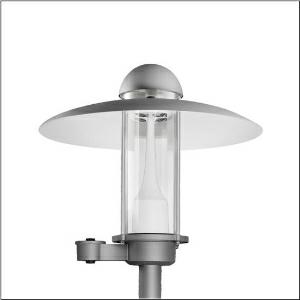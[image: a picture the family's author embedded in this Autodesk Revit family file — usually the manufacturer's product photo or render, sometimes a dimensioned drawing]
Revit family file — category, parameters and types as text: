
# Revit family: city-light_elegance___st1_2a_5xa5263er14h000032_c7d7
name_source: partatom
category: Lighting Fixtures
units: mm (PartAtom-declared; Revit-internal decimal feet)

## family parameters
Cut with Voids When Loaded = No
Host = Face
Light Source = No
Part Type = Normal
Room Calculation Point = No
Round Connector Dimension = Use Diameter
Shared = No

## types (1)
- --- (1 x LED, 1470 lm, 14.2 W, 3000K)
    Apparent Load = 14 VA
    CIE Flux Codes = 22 62 94 98 100
    Color Rendering = 80
    Color Temperature = 3000K
    Default Elevation = 1800 mm
    Description = City-Light Elegance, mast luminaire, Module 540 Plus, primary light control with 3 zone facetted reflector, of plastic, silver coated, highly specular, structured, primary optical cover: cover, of PMMA, transparent, light distribution: ST1.2a, light emission: direct distribution, primary light characteristic: asymmetric, installation type: post-top, LED, High Power LED, rated luminous flux: 1.470lm, luminous efficacy: 104lm/W, light colour: 730, colour temperature: 3000K, control gear: ECG Smart Interface, control: overheat protection, digital communication interface, time-dependent luminous flux control, flexible luminous flux parameterisation, presetting dimming logarithmic, with terminal, 6-pole, max. 2.5mm², mains connection: 220..240V, AC, 50/60Hz, start of lifetime: 14W, end of lifetime: 15W, reduction: 8W, luminaire housing, upper part, of aluminium, coated, Siteco® metallic grey (DB 702S), diameter: 750mm, height: 675mm, spigot size: d x l = 76 x 70mm (post-top) | with reducer (optional accessory) 60 x 70mm, post-top mast mounting element, of diecast aluminium, coated, Siteco® metallic grey (DB 702S), Module 540 Plus, traffic white (RAL 9016), protection rating (complete): IP65, insulation class (complete): insulation class II (safety insulation), certification: CE, ENEC, VDE, packaging unit: 1 piece

Light Distribution: ST1.2a
    Height = 675 mm
    Lamp = 1 x LED
    Lamp Light Flux = 1470 lm
    Lamp Power = 14.2 W
    Lamp count = 1
    Length = 750 mm
    Luminous efficacy = 104 lm/W
    Manufacturer = Siteco
    ModVariant = No
    Model = 5XA5263ER14H000032
    Number of Poles = 1
    OnlyDefault = Yes
    Power Factor = 1
    Product Name = City-Light Elegance | ST1.2a
    Product group = mast luminaire | pylon top
    ProductGroupID = 6100
    Protection Class = Protection class II
    Protection Degree = IP 65
    RLX_Detail_Level = 1
    RlxData = <blob elided: 72309 chars, md5=f19250c3>
    Socket = socket
    Standby Power = 0 W
    System Light Flux = 1470 lm
    System Power = 14 W
    Type Comments = factory setting: luminous flux: 100 % | dim-lin: 254 | 516 mA
    Type Image = l_1005991.jpg
    URL = http://relux.com
    VarID = @adj_121759
    Voltage = 0 V
    Weight = 0.00 kg
    Width = 0 mm  [stored 0 ft]

note: [stored X ft] marks values corroborated as IEEE doubles in the binary element streams (Revit-internal decimal feet)

## geometry (parser evidence)
native form markers: Blend x4, Sweep x12
no freeform markers — native parametric forms only
